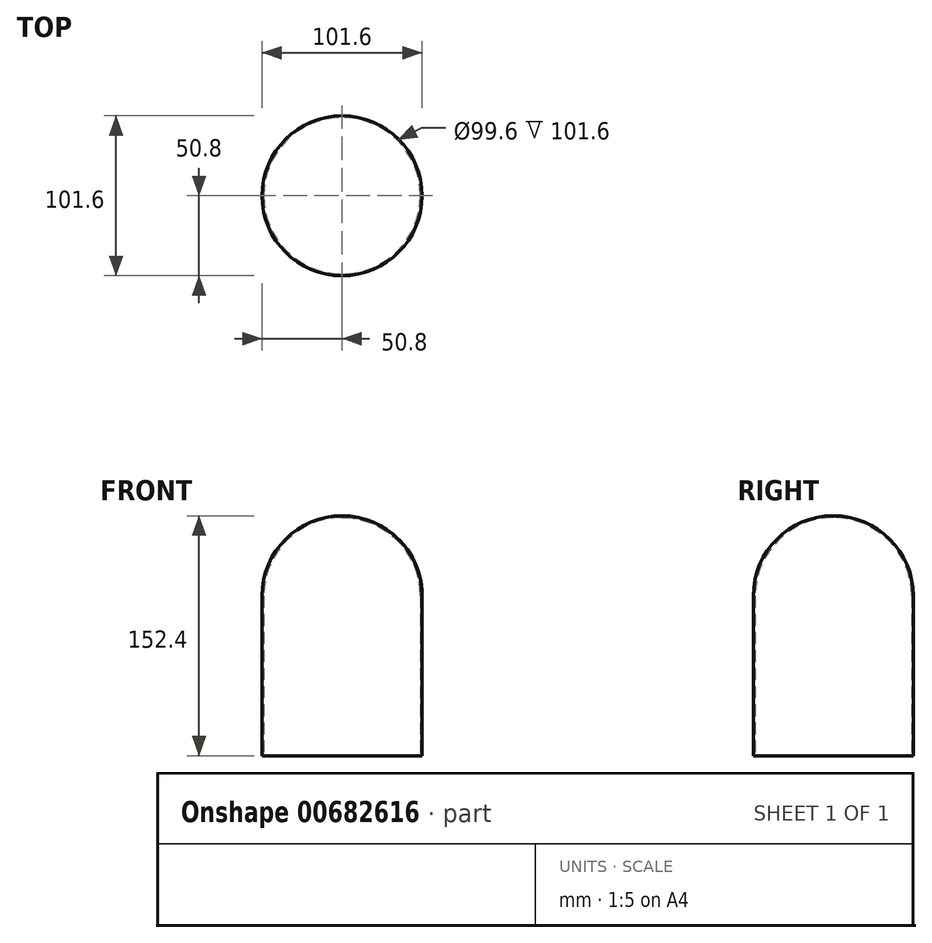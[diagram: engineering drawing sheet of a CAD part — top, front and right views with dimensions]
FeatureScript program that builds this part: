
annotation { "Feature Type Name" : "Feature", "Feature Type Description" : "" }
export const myFeature = defineFeature(function(context is Context, id is Id, definition is map)
    precondition{}
    {
        {
            var Q0;
            Q0=qCreatedBy(makeId("Top.planeOp"),FACE);
            var sketch = newSketch(context, id + "F0", { "sketchPlane" : qUnion([Q0])});
            skCircle(sketch, "E0", {"center": v(0, 0) * mm, "radius": 50.8 * mm});
            skSolve(sketch);
        }
        {
            var Q0;
            Q0=makeQuery(id+"F0.imprint","IMPRINT",FACE,{"disambiguationData":[TD([[makeQuery(id+"F0.imprint","IMPRINT",EDGE,{"derivedFrom":sQuery(id+"F0.wireOp",EDGE,"E0")}),1.0]])]});
            extrude(context, id + "F1", {"entities" : qUnion([Q0]), "depth" : 101.6 * mm, "offsetDistance" : 25 * mm});
        }
        {
            var Q0;
            Q0=qCreatedBy(makeId("Front.planeOp"),FACE);
            var sketch = newSketch(context, id + "F2", { "sketchPlane" : qUnion([Q0])});
            skLineSegment(sketch, "E1", {"start": v(0, 102.41) * mm, "end": v(0, 174.63) * mm});
            skLineSegment(sketch, "E2", {"start": v(-50.8, 0) * mm, "end": v(-50.8, 101.6) * mm});
            skLineSegment(sketch, "E3", {"start": v(50.8, 101.6) * mm, "end": v(50.8, 0) * mm});
            skLineSegment(sketch, "E4.0", {"start": v(-50.8, 101.6) * mm, "end": v(50.8, 101.6) * mm});
            skLineSegment(sketch, "E5", {"start": v(0, 102.41) * mm, "end": v(0, 99.8) * mm});
            skPoint(sketch, "E6", {"position": v(0, 101.6) * mm});
            skArc(sketch, "E7", {"start": v(50.8, 101.6) * mm, "mid": v(35.92, 137.52) * mm, "end": v(0, 152.4) * mm});
            skSolve(sketch);
        }
        {
            var Q0;
            {var subQ3=sQuery(id+"F2.wireOp",EDGE,"E7");Q0=makeQuery(id+"F2.imprint","IMPRINT",FACE,{"disambiguationData":[TD([[makeQuery(id+"F2.imprint","IMPRINT",EDGE,{"derivedFrom":subQ3}),1.0]])]});}
            var Q1;
            Q1=sQuery(id+"F2.wireOp",EDGE,"E1");
            revolve(context, id + "F3", {"operationType" : NewBodyOperationType.ADD, "surfaceOperationType" : NewSurfaceOperationType.NEW, "entities" : qUnion([Q0]), "axis" : qUnion([Q1]), "revolveType" : RevolveType.FULL});
        }
        {
            var Q0;
            Q0=makeQuery(id+"F1.opExtrude","CAP_FACE",FACE,{"disambiguationData":[OSD([sQuery(id+"F0.wireOp",EDGE,"E0")])],"isStart":true});
            shell(context, id + "F4", {"entities" : qUnion([Q0]), "thickness" : 1 * mm});
        }
    });
